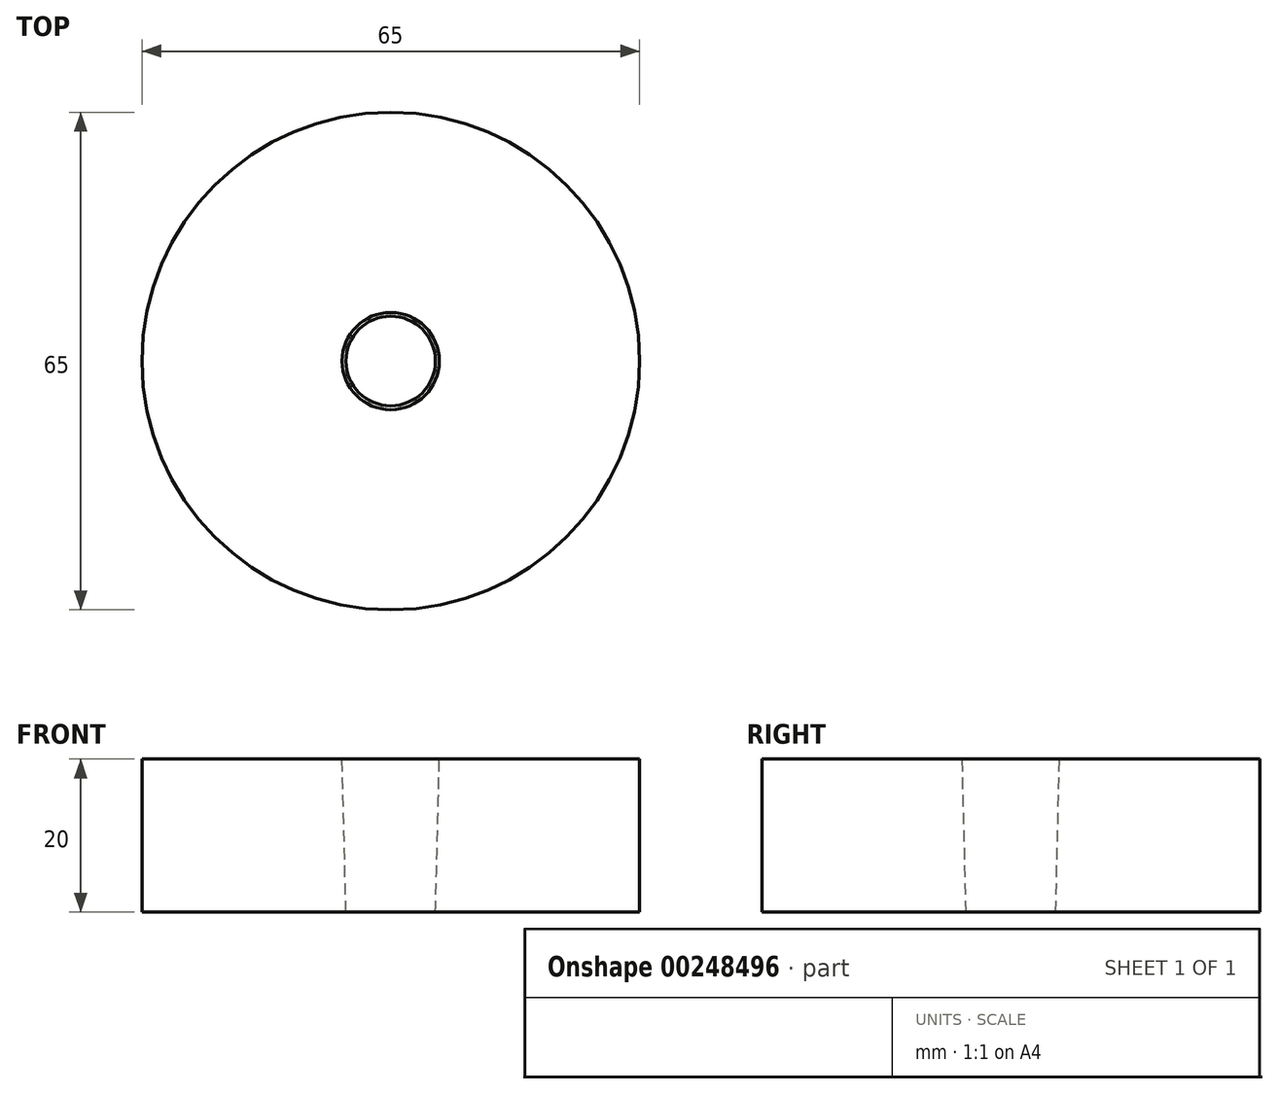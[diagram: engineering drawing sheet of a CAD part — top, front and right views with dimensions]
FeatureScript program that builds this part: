
annotation { "Feature Type Name" : "Feature", "Feature Type Description" : "" }
export const myFeature = defineFeature(function(context is Context, id is Id, definition is map)
    precondition{}
    {
        {
            var Q0;
            Q0=qCreatedBy(makeId("Top.planeOp"),FACE);
            var sketch = newSketch(context, id + "F0", { "sketchPlane" : qUnion([Q0])});
            skCircle(sketch, "E0", {"center": v(0, 0) * mm, "radius": 32.5 * mm});
            skCircle(sketch, "E1", {"center": v(0, 0) * mm, "radius": 5.85 * mm});
            skSolve(sketch);
        }
        {
            var Q0;
            Q0=makeQuery(id+"F0.imprint","IMPRINT",FACE,{"disambiguationData":[TD([[makeQuery(id+"F0.imprint","IMPRINT",EDGE,{"derivedFrom":sQuery(id+"F0.wireOp",EDGE,"E0")}),1.0]])]});
            extrude(context, id + "F1", {"entities" : qUnion([Q0]), "depth" : 20 * mm});
        }
        {
            var Q0;
            Q0=makeQuery(id+"F1.opExtrude","CAP_EDGE",EDGE,{"disambiguationData":[OSD([sQuery(id+"F0.wireOp",EDGE,"E1")])],"isStart":false});
            chamfer(context, id + "F2", {"entities" : qUnion([Q0]), "chamferType" : ChamferType.TWO_OFFSETS, "width1" : 20 * mm, "oppositeDirection" : false, "width2" : .5 * mm, "tangentPropagation" : true});
        }
    });
